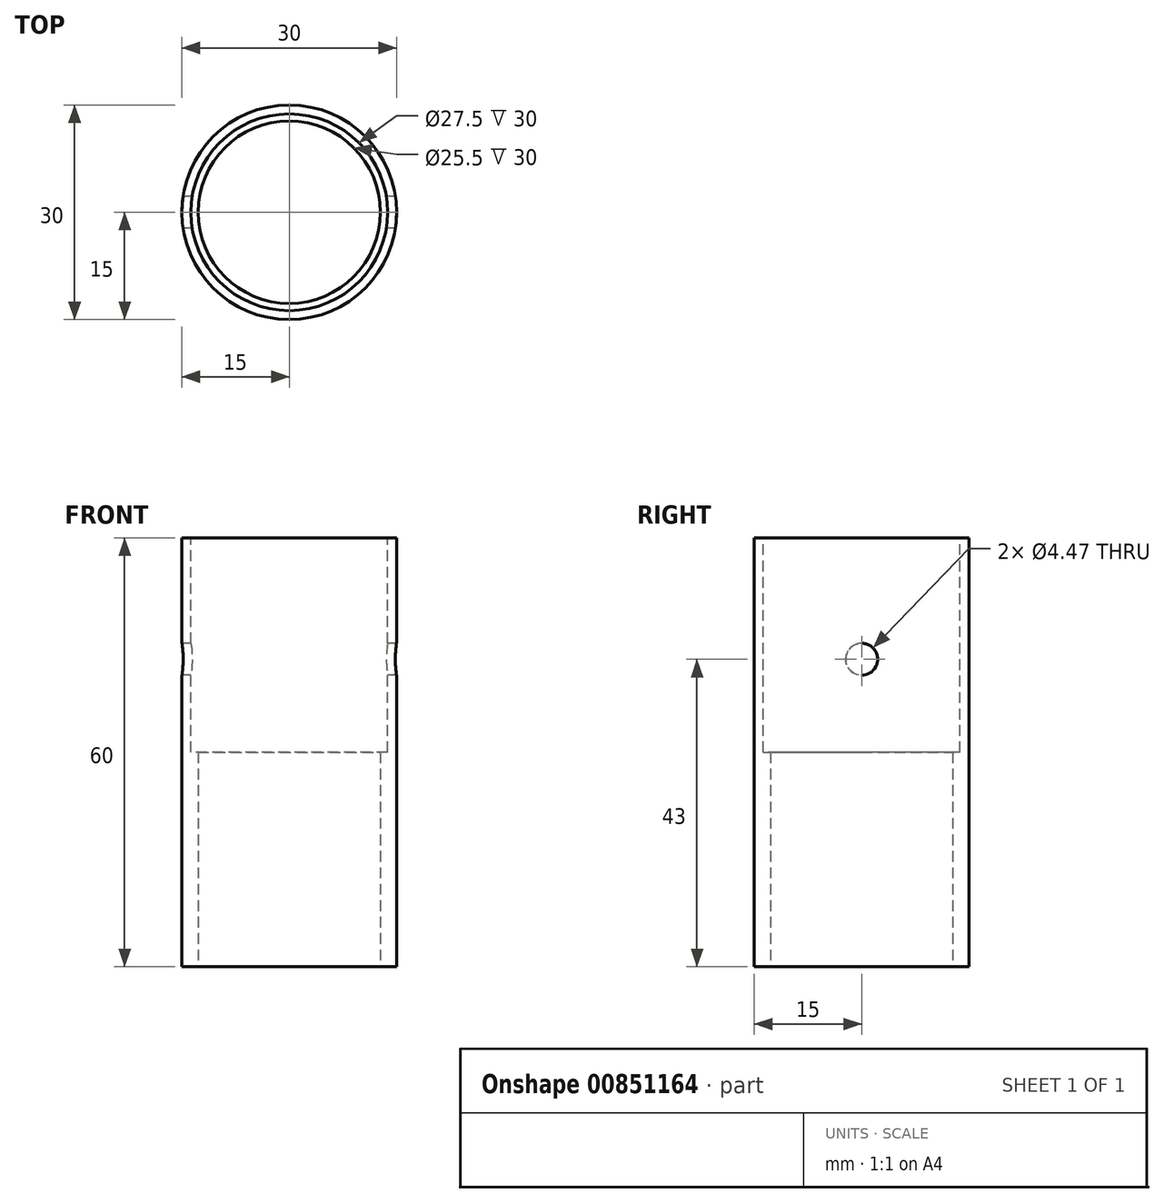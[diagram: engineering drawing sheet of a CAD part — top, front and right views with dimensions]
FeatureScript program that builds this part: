
annotation { "Feature Type Name" : "Feature", "Feature Type Description" : "" }
export const myFeature = defineFeature(function(context is Context, id is Id, definition is map)
    precondition{}
    {
        {
            var Q0;
            Q0=qCreatedBy(makeId("Top.planeOp"),FACE);
            var sketch = newSketch(context, id + "F0", { "sketchPlane" : qUnion([Q0])});
            skCircle(sketch, "E0", {"center": v(0, 0) * mm, "radius": 15 * mm});
            skCircle(sketch, "E1", {"center": v(0, 0) * mm, "radius": 13.5 * mm});
            skCircle(sketch, "E2", {"center": v(0, 0) * mm, "radius": 12.5 * mm});
            skSolve(sketch);
        }
        {
            var Q0;
            Q0=makeQuery(id+"F0.imprint","IMPRINT",FACE,{"disambiguationData":[TD([[makeQuery(id+"F0.imprint","IMPRINT",EDGE,{"derivedFrom":sQuery(id+"F0.wireOp",EDGE,"E0")}),1.0]])]});
            extrude(context, id + "F1", {"entities" : qUnion([Q0]), "depth" : 30 * mm, "offsetDistance" : 25 * mm});
        }
        {
            var Q0;
            Q0=makeQuery(id+"F0.imprint","IMPRINT",FACE,{"disambiguationData":[TD([[makeQuery(id+"F0.imprint","IMPRINT",EDGE,{"derivedFrom":sQuery(id+"F0.wireOp",EDGE,"E1")}),1.0]])]});
            var Q1;
            Q1=makeQuery(id+"F0.imprint","IMPRINT",FACE,{"disambiguationData":[TD([[makeQuery(id+"F0.imprint","IMPRINT",EDGE,{"derivedFrom":sQuery(id+"F0.wireOp",EDGE,"E0")}),1.0]])]});
            extrude(context, id + "F2", {"entities" : qUnion([Q0, Q1]), "operationType" : NewBodyOperationType.ADD, "oppositeDirection" : true, "depth" : 30 * mm, "offsetDistance" : 25 * mm});
        }
        {
            var Q0;
            Q0=qCreatedBy(makeId("Right.planeOp"),FACE);
            var sketch = newSketch(context, id + "F3", { "sketchPlane" : qUnion([Q0])});
            skCircle(sketch, "E3", {"center": v(0, 13) * mm, "radius": 2.23 * mm});
            skSolve(sketch);
        }
        {
            var Q0;
            Q0 = qSketchRegion(id + "F3", true);
            extrude(context, id + "F4", {"entities" : qUnion([Q0]), "operationType" : NewBodyOperationType.REMOVE, "endBound" : BoundingType.SYMMETRIC, "depth" : 100 * mm, "offsetDistance" : 25 * mm});
        }
        {
            var Q0;
            Q0=makeQuery(id+"F1.opExtrude","CAP_FACE",FACE,{"disambiguationData":[OSD([sQuery(id+"F0.wireOp",EDGE,"E0"),sQuery(id+"F0.wireOp",EDGE,"E1")])],"isStart":false});
            var sketch = newSketch(context, id + "F5", { "sketchPlane" : qUnion([Q0])});
            skCircle(sketch, "E4", {"center": v(0, 0) * mm, "radius": 13.75 * mm});
            skSolve(sketch);
        }
        {
            var Q0;
            Q0 = qSketchRegion(id + "F5", true);
            extrude(context, id + "F6", {"entities" : qUnion([Q0]), "operationType" : NewBodyOperationType.REMOVE, "oppositeDirection" : true, "depth" : 30 * mm, "offsetDistance" : 25 * mm});
        }
        {
            var Q0;
            Q0=makeQuery(id+"F2.opExtrude","CAP_FACE",FACE,{"disambiguationData":[OSD([sQuery(id+"F0.wireOp",EDGE,"E0"),sQuery(id+"F0.wireOp",EDGE,"E2")])],"isStart":false});
            var sketch = newSketch(context, id + "F7", { "sketchPlane" : qUnion([Q0])});
            skCircle(sketch, "E5", {"center": v(0, 0) * mm, "radius": 12.75 * mm});
            skSolve(sketch);
        }
        {
            var Q0;
            Q0 = qSketchRegion(id + "F7", true);
            extrude(context, id + "F8", {"entities" : qUnion([Q0]), "operationType" : NewBodyOperationType.REMOVE, "oppositeDirection" : true, "depth" : 30 * mm, "offsetDistance" : 25 * mm});
        }
    });
